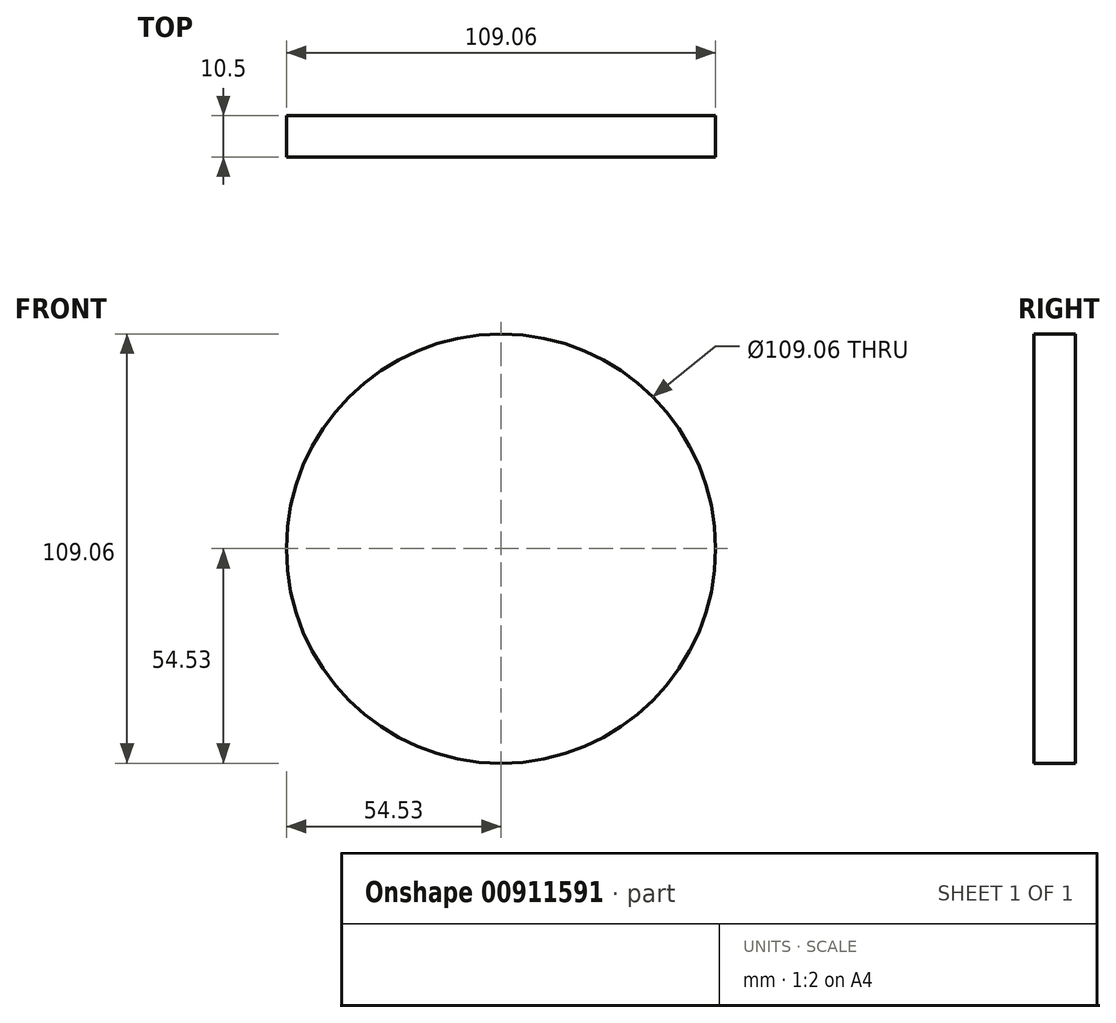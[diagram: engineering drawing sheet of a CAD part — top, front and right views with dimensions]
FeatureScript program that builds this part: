
annotation { "Feature Type Name" : "Feature", "Feature Type Description" : "" }
export const myFeature = defineFeature(function(context is Context, id is Id, definition is map)
    precondition{}
    {
        {
            var Q0;
            Q0=qCreatedBy(makeId("Front.planeOp"),FACE);
            var sketch = newSketch(context, id + "F0", { "sketchPlane" : qUnion([Q0])});
            skCircle(sketch, "E0", {"center": v(0, 0) * mm, "radius": 54.53 * mm});
            skSolve(sketch);
        }
        {
            var Q0;
            Q0=sQuery(id+"F0.wireOp",EDGE,"E0");
            extrude(context, id + "F1", {"bodyType" : ToolBodyType.SURFACE, "surfaceEntities" : qUnion([Q0]), "oppositeDirection" : true, "depth" : 10.5 * mm, "offsetDistance" : 25.4 * mm});
        }
    });
